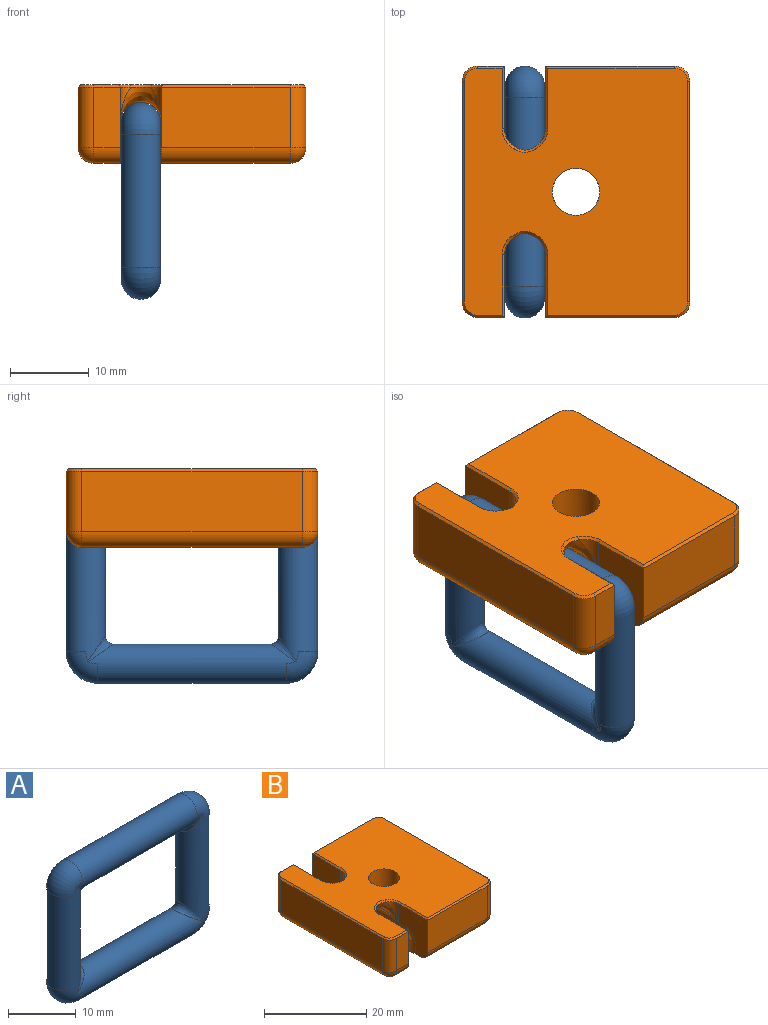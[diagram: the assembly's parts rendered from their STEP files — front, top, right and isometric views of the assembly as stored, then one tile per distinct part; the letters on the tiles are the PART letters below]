
ASSEMBLY  parts=2 mates=1
PART A: 12 faces, bbox 32x5x25 mm
  f0: cylinder r=2.5mm len=26.35mm, axis (-1,0,0), area 365mm2, adj f4,f5,f10,f11
  f1: cylinder r=2.5mm len=19.35mm, axis (0,0,-1), area 255.1mm2, adj f4,f7,f8,f10
  f2: cylinder r=2.5mm len=19.35mm, axis (0,0,1), area 255.1mm2, adj f5,f6,f9,f11
  f3: cylinder r=2.5mm len=26.35mm, axis (1,0,0), area 365mm2, adj f6,f7,f8,f9
  f4: bspline ~5x3.5mm, area 8.9mm2, adj f0,f1,f10
  f5: bspline ~5x3.5mm, area 8.9mm2, adj f0,f2,f11
  f6: bspline ~5x3.5mm, area 8.9mm2, adj f2,f3,f9
  f7: bspline ~5x3.5mm, area 8.9mm2, adj f1,f3,f8
  f8: torus R=1.5mm, axis (0,-1,0), area 37.7mm2, adj f1,f3,f7
  f9: torus R=1.5mm, axis (0,-1,0), area 37.7mm2, adj f2,f3,f6
  f10: torus R=1.5mm, axis (0,-1,0), area 37.7mm2, adj f0,f1,f4
  f11: torus R=1.5mm, axis (0,-1,0), area 37.7mm2, adj f0,f2,f5
PART B: 79 faces, bbox 29.1x32.1x12 mm
  f0: cylinder r=2.6mm len=4.5mm, axis (0,0,1), area 6.3mm2, adj f16,f58,f60
  f1: cylinder r=2.6mm len=4.5mm, axis (0,0,1), area 6.3mm2, adj f12,f57,f77
  f2: plane 31.46x28.46mm, normal (0,0,1), area 745mm2, adj f17,f59,f60,f61,f62,f63,f64,f65
  f3: cylinder r=2.6mm len=20mm, axis (0,-1,0), area 222.4mm2, adj f12,f13,f15,f16,f43,f44,f45,f46
  f4: plane 7.7x3.4mm, normal (0,-1,0), area 26.2mm2, adj f16,f23,f25,f61
  f5: plane 16.4x7.7mm, normal (0,1,0), area 126.3mm2, adj f12,f29,f32,f76
  f6: plane 28x7.7mm, normal (1,0,0), area 215.6mm2, adj f27,f30,f32,f72
  f7: plane 7.7x3.4mm, normal (0,1,0), area 26.2mm2, adj f13,f19,f20,f69
  f8: plane 28x7.7mm, normal (-1,0,0), area 215.6mm2, adj f20,f22,f23,f65
  f9: plane 16.4x7.7mm, normal (0,-1,0), area 126.3mm2, adj f15,f26,f27,f68
  f10: plane 28x25mm, normal (0,0,-1), area 585.2mm2, adj f11,f12,f13,f14,f15,f16,f18,f19
  f11: plane 0.2x0.1mm, normal (0,1,0), area 0mm2, adj f10,f37,f39,f53
  f12: plane 9.7x8mm, normal (-1,0,0), area 54.9mm2, adj f1,f3,f5,f10,f29,f37,f38,f78
  f13: plane 9.7x8mm, normal (1,0,0), area 54.9mm2, adj f3,f7,f10,f19,f39,f40,f42,f71
  f14: plane 0.2x0.1mm, normal (0,-1,0), area 0mm2, adj f10,f33,f35,f46
  f15: plane 9.7x8mm, normal (-1,0,0), area 54.9mm2, adj f3,f9,f10,f26,f33,f34,f41,f66
  f16: plane 9.7x8mm, normal (1,0,0), area 54.9mm2, adj f0,f3,f4,f10,f25,f35,f36,f59
  f17: cylinder r=3mm len=8mm, axis (0,0,-1), area 150.8mm2, adj f2,f18
  f18: cone r=3mm half-angle=45deg, axis (0,0,-1), area 71.1mm2, adj f10,f17
  f19: cylinder r=2mm len=3.4mm, axis (-1,0,0), area 10.7mm2, adj f7,f10,f13,f21
  f20: cylinder r=2mm len=7.7mm, axis (0,0,-1), area 24.2mm2, adj f7,f8,f21,f67
  f21: sphere r=2mm, area 8.6mm2, adj f19,f20,f22
  f22: cylinder r=2mm len=28mm, axis (0,-1,0), area 88mm2, adj f8,f10,f21,f24
  f23: cylinder r=2mm len=7.7mm, axis (0,0,1), area 24.2mm2, adj f4,f8,f24,f63
  f24: sphere r=2mm, area 6.3mm2, adj f22,f23,f25
  f25: cylinder r=2mm len=3.4mm, axis (1,0,0), area 10.7mm2, adj f4,f10,f16,f24
  f26: cylinder r=2mm len=16.4mm, axis (1,0,0), area 51.5mm2, adj f9,f10,f15,f28
  f27: cylinder r=2mm len=7.7mm, axis (0,0,-1), area 24.2mm2, adj f6,f9,f28,f70
  f28: sphere r=2mm, area 8.6mm2, adj f26,f27,f30
  f29: cylinder r=2mm len=16.4mm, axis (-1,0,0), area 51.5mm2, adj f5,f10,f12,f31
  f30: cylinder r=2mm len=28mm, axis (0,1,0), area 88mm2, adj f6,f10,f28,f31
  f31: sphere r=2mm, area 4mm2, adj f29,f30,f32
  f32: cylinder r=2mm len=7.7mm, axis (0,0,1), area 24.2mm2, adj f5,f6,f31,f74
  f33: cylinder r=2.5mm len=2.6mm, axis (0,0,-1), area 6mm2, adj f10,f14,f15,f34,f45
  f34: bspline ~2.87x2.51mm, area 3.9mm2, adj f15,f33,f43,f44
  f35: cylinder r=2.5mm len=2.6mm, axis (0,0,1), area 6mm2, adj f10,f14,f16,f36,f47
  f36: bspline ~2.87x2.51mm, area 3.8mm2, adj f16,f35,f48,f49
  f37: cylinder r=2.5mm len=2.6mm, axis (0,0,-1), area 6mm2, adj f10,f11,f12,f38,f52
  f38: bspline ~2.87x2.51mm, area 3.8mm2, adj f12,f37,f50,f51
  f39: cylinder r=2.5mm len=2.6mm, axis (0,0,1), area 6mm2, adj f10,f11,f13,f40,f54
  f40: bspline ~2.87x2.51mm, area 3.9mm2, adj f13,f39,f55,f56
  f41: cylinder r=2.6mm len=4.5mm, axis (0,0,1), area 6.3mm2, adj f15,f58,f64
  f42: cylinder r=2.6mm len=4.5mm, axis (0,0,1), area 6.3mm2, adj f13,f57,f73
  f43: bspline ~1.07x0.24mm, area 0.1mm2, adj f3,f34,f44
  f44: bspline ~1.82x1.72mm, area 1mm2, adj f3,f34,f43,f45
  f45: bspline ~3.96x3.89mm, area 8.9mm2, adj f3,f33,f44,f46
  f46: torus R=5.1mm, axis (0,-1,0), area 0.5mm2, adj f3,f14,f45,f47
  f47: bspline ~3.96x3.89mm, area 8.8mm2, adj f3,f35,f46,f48
  f48: bspline ~1.83x1.73mm, area 1mm2, adj f3,f36,f47,f49
  f49: bspline ~1.05x0.23mm, area 0.1mm2, adj f3,f36,f48
  f50: bspline ~0.93x0.2mm, area 0.1mm2, adj f3,f38,f51
  f51: bspline ~1.83x1.73mm, area 1mm2, adj f3,f38,f50,f52
  f52: bspline ~3.96x3.89mm, area 8.8mm2, adj f3,f37,f51,f53
  f53: torus R=5.1mm, axis (0,-1,0), area 0.5mm2, adj f3,f11,f52,f54
  f54: bspline ~3.96x3.89mm, area 8.9mm2, adj f3,f39,f53,f55
  f55: bspline ~1.83x1.73mm, area 5987.9mm2, adj f3,f40,f54,f56
  f56: bspline ~1.07x0.24mm, area 0.1mm2, adj f3,f40,f55
  f57: bspline ~5.2x5.1mm, area 21.3mm2, adj f1,f3,f42,f75
  f58: bspline ~5.2x5.1mm, area 21.5mm2, adj f0,f3,f41,f62
  f59: plane 8x0.3mm, normal (0.71,0,0.71), area 3.3mm2, adj f2,f16,f60,f61
  f60: cone r=2.6mm half-angle=45deg, axis (0,0,1), area 1.3mm2, adj f0,f2,f59,f62
  f61: plane 3.4x0.3mm, normal (0,-0.71,0.71), area 1.4mm2, adj f2,f4,f59,f63
  f62: bspline ~2.73x0.69mm, area 1.3mm2, adj f2,f58,f60,f64
  f63: cone r=1.7mm half-angle=45deg, axis (0,0,-1), area 1.2mm2, adj f2,f23,f61,f65
  f64: cone r=2.6mm half-angle=45deg, axis (0,0,1), area 1.3mm2, adj f2,f41,f62,f66
  f65: plane 28x0.3mm, normal (-0.71,0,0.71), area 11.9mm2, adj f2,f8,f63,f67
  f66: plane 8x0.3mm, normal (-0.71,0,0.71), area 3.3mm2, adj f2,f15,f64,f68
  f67: cone r=1.7mm half-angle=45deg, axis (0,0,-1), area 1.2mm2, adj f2,f20,f65,f69
  f68: plane 16.4x0.3mm, normal (0,-0.71,0.71), area 6.9mm2, adj f2,f9,f66,f70
  f69: plane 3.4x0.3mm, normal (0,0.71,0.71), area 1.4mm2, adj f2,f7,f67,f71
  f70: cone r=1.7mm half-angle=45deg, axis (0,0,-1), area 1.2mm2, adj f2,f27,f68,f72
  f71: plane 8x0.3mm, normal (0.71,0,0.71), area 3.3mm2, adj f2,f13,f69,f73
  f72: plane 28x0.3mm, normal (0.71,0,0.71), area 11.9mm2, adj f2,f6,f70,f74
  f73: cone r=2.6mm half-angle=45deg, axis (0,0,1), area 1.3mm2, adj f2,f42,f71,f75
  f74: cone r=1.7mm half-angle=45deg, axis (0,0,-1), area 1.2mm2, adj f2,f32,f72,f76
  f75: bspline ~2.73x0.69mm, area 1.3mm2, adj f2,f57,f73,f77
  f76: plane 16.4x0.3mm, normal (0,0.71,0.71), area 6.9mm2, adj f2,f5,f74,f78
  f77: cone r=2.6mm half-angle=45deg, axis (0,0,1), area 1.3mm2, adj f1,f2,f75,f78
  f78: plane 8x0.3mm, normal (-0.71,0,0.71), area 3.3mm2, adj f2,f12,f76,f77
PLACE A rot(axis=(0,0,-1),90deg) t=(-4,0,-14.8)mm
PLACE B t=(0,0,-10)mm
MATE fastened A.f0 <-> B.f3  axis (0,1,0) through (-6.5,0,-4.8)mm
